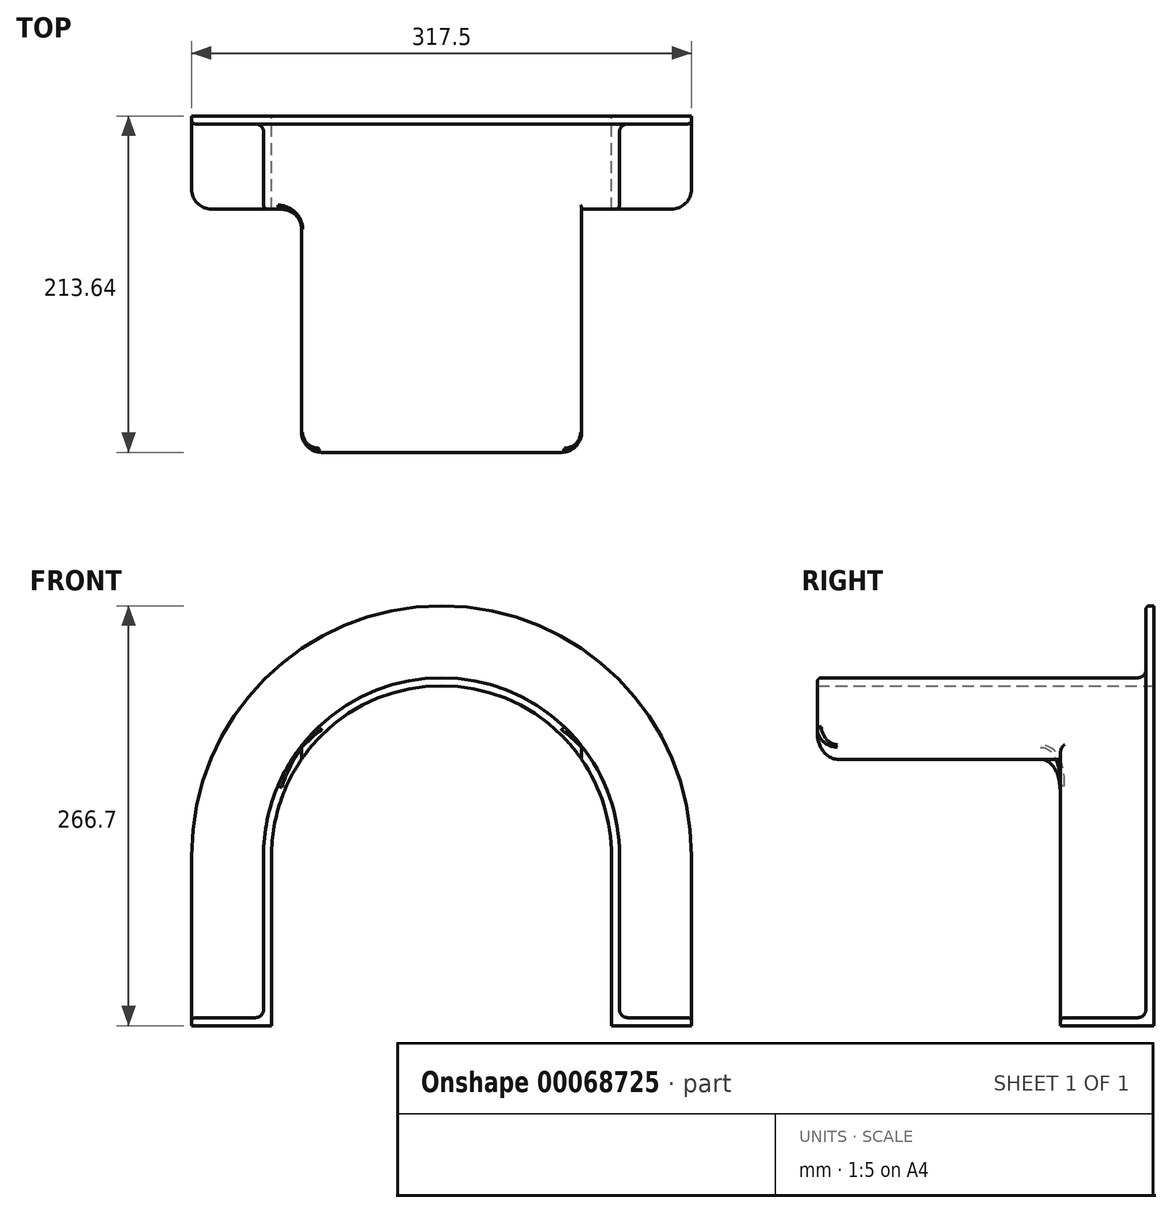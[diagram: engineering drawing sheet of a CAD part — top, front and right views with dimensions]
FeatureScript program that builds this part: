
annotation { "Feature Type Name" : "Feature", "Feature Type Description" : "" }
export const myFeature = defineFeature(function(context is Context, id is Id, definition is map)
    precondition{}
    {
        {
            var Q0;
            Q0=qCreatedBy(makeId("Front.planeOp"),FACE);
            var sketch = newSketch(context, id + "F0", { "sketchPlane" : qUnion([Q0])});
            skLineSegment(sketch, "E0.rect.bottom", {"start": v(-158.75, -53.98) * mm, "end": v(-107.95, -53.98) * mm});
            skLineSegment(sketch, "E0.rect.top", {"start": v(-107.95, 53.97) * mm, "end": v(107.95, 53.97) * mm, "construction": true});
            skLineSegment(sketch, "E0.rect.left", {"start": v(-107.95, -53.98) * mm, "end": v(-107.95, 53.98) * mm});
            skLineSegment(sketch, "E0.rect.right", {"start": v(107.95, -53.98) * mm, "end": v(107.95, 53.97) * mm});
            skPoint(sketch, "E0.rect.middle", {"position": v(0, 0) * mm});
            skLineSegment(sketch, "E1.0", {"start": v(158.75, -53.98) * mm, "end": v(158.75, 53.97) * mm});
            skArc(sketch, "E1.1", {"start": v(-158.75, 53.97) * mm, "mid": v(0, 212.72) * mm, "end": v(158.75, 53.98) * mm});
            skLineSegment(sketch, "E1.2", {"start": v(-158.75, -53.98) * mm, "end": v(-158.75, 53.97) * mm});
            skLineSegment(sketch, "E2.trimOffspring", {"start": v(107.95, -53.98) * mm, "end": v(158.75, -53.98) * mm});
            skCircle(sketch, "E3.converted", {"center": v(0, 53.97) * mm, "radius": 107.95 * mm});
            skLineSegment(sketch, "E4", {"start": v(-107.95, -53.98) * mm, "end": v(107.95, -53.98) * mm, "construction": true});
            skSolve(sketch);
        }
        {
            var Q0;
            Q0=qCreatedBy(makeId("Front.planeOp"),FACE);
            var sketch = newSketch(context, id + "F1", { "sketchPlane" : qUnion([Q0])});
            skArc(sketch, "E5.0", {"start": v(-107.95, 53.98) * mm, "mid": v(0, 161.92) * mm, "end": v(107.95, 53.97) * mm});
            skLineSegment(sketch, "E5.1", {"start": v(-158.75, -53.98) * mm, "end": v(-107.95, -53.98) * mm});
            skLineSegment(sketch, "E5.3", {"start": v(-107.95, -53.98) * mm, "end": v(-107.95, 53.98) * mm});
            skLineSegment(sketch, "E5.4", {"start": v(107.95, -53.98) * mm, "end": v(107.95, 53.97) * mm});
            skPoint(sketch, "E5.5", {"position": v(0, 0) * mm});
            skLineSegment(sketch, "E5.6", {"start": v(158.75, -53.98) * mm, "end": v(158.75, 53.97) * mm});
            skArc(sketch, "E5.7", {"start": v(-158.75, 53.97) * mm, "mid": v(0, 212.72) * mm, "end": v(158.75, 53.98) * mm});
            skLineSegment(sketch, "E5.8", {"start": v(-158.75, -53.98) * mm, "end": v(-158.75, 53.97) * mm});
            skLineSegment(sketch, "E5.9", {"start": v(107.95, -53.98) * mm, "end": v(158.75, -53.98) * mm});
            skArc(sketch, "E5.10", {"start": v(-107.95, 53.98) * mm, "mid": v(0, 161.92) * mm, "end": v(107.95, 53.97) * mm});
            skPoint(sketch, "E6.orphan", {"position": v(-107.95, 53.97) * mm});
            skPoint(sketch, "E5.2.end.orphan", {"position": v(107.95, 53.97) * mm});
            skPoint(sketch, "E7.orphan", {"position": v(107.95, -53.98) * mm});
            skPoint(sketch, "E5.11.start.orphan", {"position": v(-107.95, -53.98) * mm});
            skSolve(sketch);
        }
        {
            var Q0;
            Q0 = qSketchRegion(id + "F1", true);
            extrude(context, id + "F2", {"entities" : qUnion([Q0]), "depth" : 59.24 * mm});
        }
        {
            var Q0;
            Q0=makeQuery(id+"F2.opExtrude","CAP_FACE",FACE,{"disambiguationData":[OSD([sQuery(id+"F1.wireOp",EDGE,"E5.1"),sQuery(id+"F1.wireOp",EDGE,"E5.3"),sQuery(id+"F1.wireOp",EDGE,"E5.4"),sQuery(id+"F1.wireOp",EDGE,"E5.6"),sQuery(id+"F1.wireOp",EDGE,"E5.7"),sQuery(id+"F1.wireOp",EDGE,"E5.8"),sQuery(id+"F1.wireOp",EDGE,"E5.9"),sQuery(id+"F1.wireOp",EDGE,"E5.10")])],"isStart":false});
            var Q1;
            Q1=makeQuery(id+"F2.opExtrude","SWEPT_FACE",FACE,{"disambiguationData":[OSD([sQuery(id+"F1.wireOp",EDGE,"E5.7")])]});
            var Q2;
            Q2=makeQuery(id+"F2.opExtrude","SWEPT_FACE",FACE,{"disambiguationData":[OSD([sQuery(id+"F1.wireOp",EDGE,"E5.8")])]});
            var Q3;
            Q3=makeQuery(id+"F2.opExtrude","SWEPT_FACE",FACE,{"disambiguationData":[OSD([sQuery(id+"F1.wireOp",EDGE,"E5.6")])]});
            shell(context, id + "F3", {"entities" : qUnion([Q0, Q1, Q2, Q3]), "thickness" : 5.08 * mm});
        }
        {
            var Q0;
            Q0=makeQuery(id+"F2.opExtrude","CAP_EDGE",EDGE,{"disambiguationData":[OSD([sQuery(id+"F1.wireOp",EDGE,"E5.8")])],"isStart":false});
            var Q1;
            Q1=makeQuery(id+"F2.opExtrude","CAP_EDGE",EDGE,{"disambiguationData":[OSD([sQuery(id+"F1.wireOp",EDGE,"E5.6")])],"isStart":false});
            fillet(context, id + "F4", {"entities" : qUnion([Q0, Q1]), "radius" : 12.7 * mm, "tangentPropagation" : true, "allowEdgeOverflow" : false});
        }
        {
            var Q0;
            Q0=makeQuery(id+"F3.opShell","OFFSET_EDGE",EDGE,{"disambiguationData":[OSD([sQuery(id+"F1.wireOp",EDGE,"E5.1"),sQuery(id+"F1.wireOp",EDGE,"E5.3")])]});
            var Q1;
            {var subQ0=sQuery(id+"F1.wireOp",EDGE,"E5.1");Q1=makeQuery(id+"F3.opShell","OFFSET_EDGE",EDGE,{"disambiguationData":[OSD([subQ0]),TDD([makeQuery(id+"F2.opExtrude","CAP_EDGE",EDGE,{"disambiguationData":[OSD([subQ0])],"isStart":true})])]});}
            var Q2;
            {var subQ0=sQuery(id+"F1.wireOp",EDGE,"E5.3");Q2=makeQuery(id+"F3.opShell","OFFSET_EDGE",EDGE,{"disambiguationData":[OSD([subQ0]),TDD([makeQuery(id+"F2.opExtrude","CAP_EDGE",EDGE,{"disambiguationData":[OSD([subQ0])],"isStart":true})])]});}
            var Q3;
            {var subQ0=sQuery(id+"F1.wireOp",EDGE,"E5.9");Q3=makeQuery(id+"F3.opShell","OFFSET_EDGE",EDGE,{"disambiguationData":[OSD([subQ0]),TDD([makeQuery(id+"F2.opExtrude","CAP_EDGE",EDGE,{"disambiguationData":[OSD([subQ0])],"isStart":true})])]});}
            var Q4;
            Q4=makeQuery(id+"F3.opShell","OFFSET_EDGE",EDGE,{"disambiguationData":[OSD([sQuery(id+"F1.wireOp",EDGE,"E5.4"),sQuery(id+"F1.wireOp",EDGE,"E5.9")])]});
            fillet(context, id + "F5", {"entities" : qUnion([Q0, Q1, Q2, Q3, Q4]), "radius" : 5.08 * mm, "tangentPropagation" : true, "allowEdgeOverflow" : false});
        }
        {
            var Q0;
            Q0=makeQuery(id+"F2.opExtrude","CAP_FACE",FACE,{"disambiguationData":[OSD([sQuery(id+"F1.wireOp",EDGE,"E5.1"),sQuery(id+"F1.wireOp",EDGE,"E5.3"),sQuery(id+"F1.wireOp",EDGE,"E5.4"),sQuery(id+"F1.wireOp",EDGE,"E5.6"),sQuery(id+"F1.wireOp",EDGE,"E5.7"),sQuery(id+"F1.wireOp",EDGE,"E5.8"),sQuery(id+"F1.wireOp",EDGE,"E5.9"),sQuery(id+"F1.wireOp",EDGE,"E5.10")])],"isStart":false});
            var sketch = newSketch(context, id + "F6", { "sketchPlane" : qUnion([Q0])});
            skArc(sketch, "E8.0", {"start": v(-88.9, 123.78) * mm, "mid": v(0, 167) * mm, "end": v(88.9, 123.78) * mm});
            skArc(sketch, "E8.1", {"start": v(-88.9, 115.21) * mm, "mid": v(0, 161.93) * mm, "end": v(88.9, 115.21) * mm});
            skLineSegment(sketch, "E9", {"start": v(-88.9, 115.21) * mm, "end": v(88.9, 115.21) * mm, "construction": true});
            skLineSegment(sketch, "E10", {"start": v(88.9, 115.21) * mm, "end": v(88.9, 123.78) * mm});
            skLineSegment(sketch, "E11", {"start": v(-88.9, 115.21) * mm, "end": v(-88.9, 123.78) * mm});
            skPoint(sketch, "E12.orphan", {"position": v(113.03, 53.98) * mm});
            skPoint(sketch, "E13.orphan", {"position": v(107.95, 53.97) * mm});
            skPoint(sketch, "E14.orphan", {"position": v(-107.95, 53.98) * mm});
            skPoint(sketch, "E15.orphan", {"position": v(-113.03, 53.98) * mm});
            skSolve(sketch);
        }
        {
            var Q0;
            Q0 = qSketchRegion(id + "F6", true);
            extrude(context, id + "F7", {"entities" : qUnion([Q0]), "operationType" : NewBodyOperationType.ADD, "depth" : 154.4 * mm});
        }
        {
            var Q0;
            Q0=makeQuery(id+"F7.opExtrude","CAP_EDGE",EDGE,{"disambiguationData":[OSD([sQuery(id+"F6.wireOp",EDGE,"E10")])],"isStart":true});
            var Q1;
            Q1=makeQuery(id+"F7.opExtrude","CAP_EDGE",EDGE,{"disambiguationData":[OSD([sQuery(id+"F6.wireOp",EDGE,"E10")])],"isStart":false});
            var Q2;
            Q2=makeQuery(id+"F7.opExtrude","CAP_EDGE",EDGE,{"disambiguationData":[OSD([sQuery(id+"F6.wireOp",EDGE,"E11")])],"isStart":true});
            var Q3;
            Q3=makeQuery(id+"F7.opExtrude","CAP_EDGE",EDGE,{"disambiguationData":[OSD([sQuery(id+"F6.wireOp",EDGE,"E11")])],"isStart":false});
            fillet(context, id + "F8", {"entities" : qUnion([Q0, Q1, Q2, Q3]), "radius" : 12.7 * mm, "tangentPropagation" : true, "allowEdgeOverflow" : false});
        }
        {
            var Q0;
            Q0=makeQuery(id+"F7.opExtrude","CAP_EDGE",EDGE,{"disambiguationData":[OSD([sQuery(id+"F6.wireOp",EDGE,"E8.0")])],"isStart":false});
            fillet(context, id + "F9", {"entities" : qUnion([Q0]), "radius" : 2.54 * mm, "tangentPropagation" : true, "allowEdgeOverflow" : false});
        }
    });
